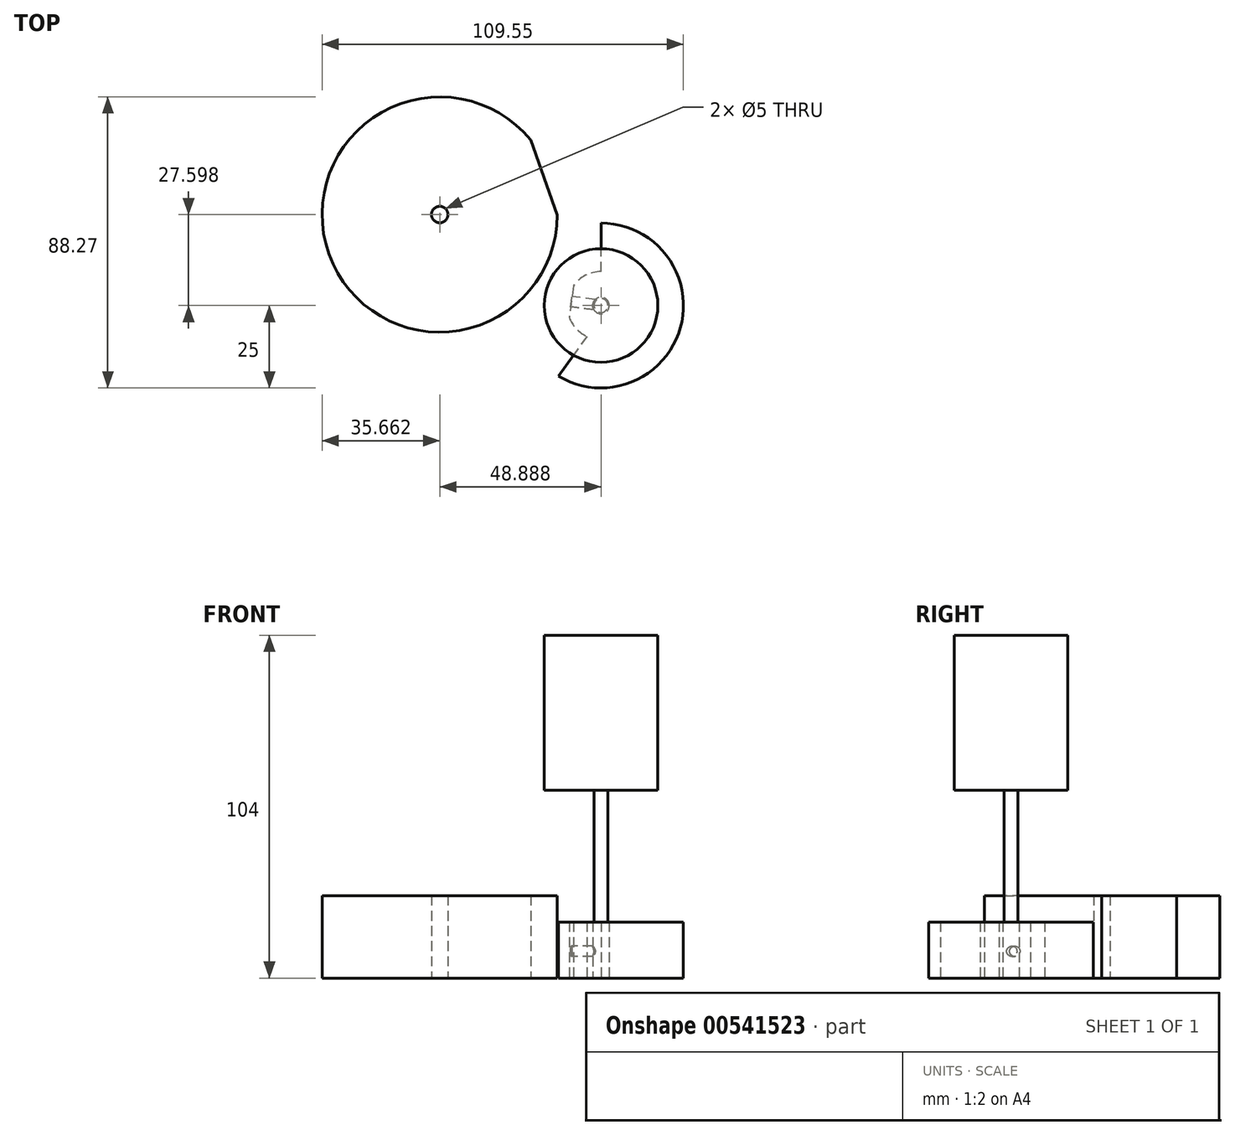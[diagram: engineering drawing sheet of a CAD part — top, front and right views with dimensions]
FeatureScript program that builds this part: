
annotation { "Feature Type Name" : "Feature", "Feature Type Description" : "" }
export const myFeature = defineFeature(function(context is Context, id is Id, definition is map)
    precondition{}
    {
        {
            var Q0;
            Q0=qCreatedBy(makeId("Top.planeOp"),FACE);
            var sketch = newSketch(context, id + "F0", { "sketchPlane" : qUnion([Q0])});
            skArc(sketch, "E0", {"start": v(-12.9, -21.42) * mm, "mid": v(24.09, -6.7) * mm, "end": v(0, 25) * mm});
            skLineSegment(sketch, "E1", {"start": v(0, 10.28) * mm, "end": v(0, 25) * mm});
            skArc(sketch, "E2", {"start": v(0, 10.28) * mm, "mid": v(-4.71, 9.14) * mm, "end": v(-8.38, 5.96) * mm});
            skLineSegment(sketch, "E3", {"start": v(-4.3, -9.34) * mm, "end": v(-12.9, -21.42) * mm});
            skCircle(sketch, "E4", {"center": v(0, 0) * mm, "radius": 2.5 * mm});
            skLineSegment(sketch, "E5", {"start": v(-8.38, 5.96) * mm, "end": v(-9.62, -3.64) * mm});
            skArc(sketch, "E6.trimOffspring", {"start": v(-9.62, -3.64) * mm, "mid": v(-7.52, -7) * mm, "end": v(-4.3, -9.34) * mm});
            skArc(sketch, "E7", {"start": v(-21.32, 50.23) * mm, "mid": v(-82.48, 15.62) * mm, "end": v(-13.22, 27.52) * mm});
            skCircle(sketch, "E8", {"center": v(-48.89, 27.6) * mm, "radius": 2.5 * mm});
            skLineSegment(sketch, "E9", {"start": v(-21.32, 50.23) * mm, "end": v(-13.22, 27.52) * mm});
            skSolve(sketch);
        }
        {
            var Q0;
            {var subQ0=sQuery(id+"F0.wireOp",EDGE,"E0");Q0=makeQuery(id+"F0.imprint","IMPRINT",FACE,{"disambiguationData":[TD([[makeQuery(id+"F0.imprint","IMPRINT",EDGE,{"derivedFrom":subQ0}),1.0]])]});}
            extrude(context, id + "F1", {"entities" : qUnion([Q0]), "depth" : 17 * mm, "offsetDistance" : 25 * mm});
        }
        {
            var Q0;
            Q0=makeQuery(id+"F1.opExtrude","CAP_FACE",FACE,{"disambiguationData":[OSD([sQuery(id+"F0.wireOp",EDGE,"E0"),sQuery(id+"F0.wireOp",EDGE,"E1"),sQuery(id+"F0.wireOp",EDGE,"E2"),sQuery(id+"F0.wireOp",EDGE,"E3"),sQuery(id+"F0.wireOp",EDGE,"E4")])],"isStart":false});
            var sketch = newSketch(context, id + "F2", { "sketchPlane" : qUnion([Q0])});
            skCircle(sketch, "E10", {"center": v(0, 0) * mm, "radius": 2.12 * mm});
            skSolve(sketch);
        }
        {
            var Q0;
            Q0=makeQuery(id+"F2.imprint","IMPRINT",FACE,{"disambiguationData":[TD([[makeQuery(id+"F2.imprint","IMPRINT",EDGE,{"derivedFrom":sQuery(id+"F2.wireOp",EDGE,"E10")}),1.0]])]});
            extrude(context, id + "F3", {"entities" : qUnion([Q0]), "depth" : 40 * mm, "offsetDistance" : 25 * mm});
        }
        {
            var Q0;
            Q0=makeQuery(id+"F3.opExtrude","CAP_FACE",FACE,{"disambiguationData":[OSD([sQuery(id+"F2.wireOp",EDGE,"E10")])],"isStart":false});
            var sketch = newSketch(context, id + "F4", { "sketchPlane" : qUnion([Q0])});
            skCircle(sketch, "E11", {"center": v(0, 0) * mm, "radius": 17.23 * mm});
            skSolve(sketch);
        }
        {
            var Q0;
            Q0=makeQuery(id+"F4.imprint","IMPRINT",FACE,{"disambiguationData":[TD([[makeQuery(id+"F4.imprint","IMPRINT",EDGE,{"derivedFrom":makeQuery(id+"F3.opExtrude","CAP_EDGE",EDGE,{"disambiguationData":[OSD([sQuery(id+"F2.wireOp",EDGE,"E10")])],"isStart":false})}),1.0]])]});
            var Q1;
            Q1=makeQuery(id+"F4.imprint","IMPRINT",FACE,{"disambiguationData":[TD([[makeQuery(id+"F4.imprint","IMPRINT",EDGE,{"derivedFrom":sQuery(id+"F4.wireOp",EDGE,"E11")}),1.0]])]});
            extrude(context, id + "F5", {"entities" : qUnion([Q0, Q1]), "operationType" : NewBodyOperationType.ADD, "depth" : 47 * mm, "offsetDistance" : 25 * mm});
        }
        {
            var Q0;
            Q0=makeQuery(id+"F1.opExtrude","SWEPT_FACE",FACE,{"disambiguationData":[OSD([sQuery(id+"F0.wireOp",EDGE,"E5")])]});
            var sketch = newSketch(context, id + "F6", { "sketchPlane" : qUnion([Q0])});
            skCircle(sketch, "E12", {"center": v(0, 8.11) * mm, "radius": 1.58 * mm});
            skSolve(sketch);
        }
        {
            var Q0;
            Q0=makeQuery(id+"F6.imprint","IMPRINT",FACE,{"disambiguationData":[TD([[makeQuery(id+"F6.imprint","IMPRINT",EDGE,{"derivedFrom":sQuery(id+"F6.wireOp",EDGE,"E12")}),1.0]])]});
            extrude(context, id + "F7", {"entities" : qUnion([Q0]), "operationType" : NewBodyOperationType.REMOVE, "endBound" : BoundingType.UP_TO_NEXT, "oppositeDirection" : true, "depth" : 25 * mm, "offsetDistance" : 25 * mm});
        }
        {
            var Q0;
            Q0=makeQuery(id+"F0.imprint","IMPRINT",FACE,{"disambiguationData":[TD([[makeQuery(id+"F0.imprint","IMPRINT",EDGE,{"derivedFrom":sQuery(id+"F0.wireOp",EDGE,"E7")}),1.0]])]});
            extrude(context, id + "F8", {"entities" : qUnion([Q0]), "depth" : 25 * mm, "offsetDistance" : 25 * mm});
        }
    });
